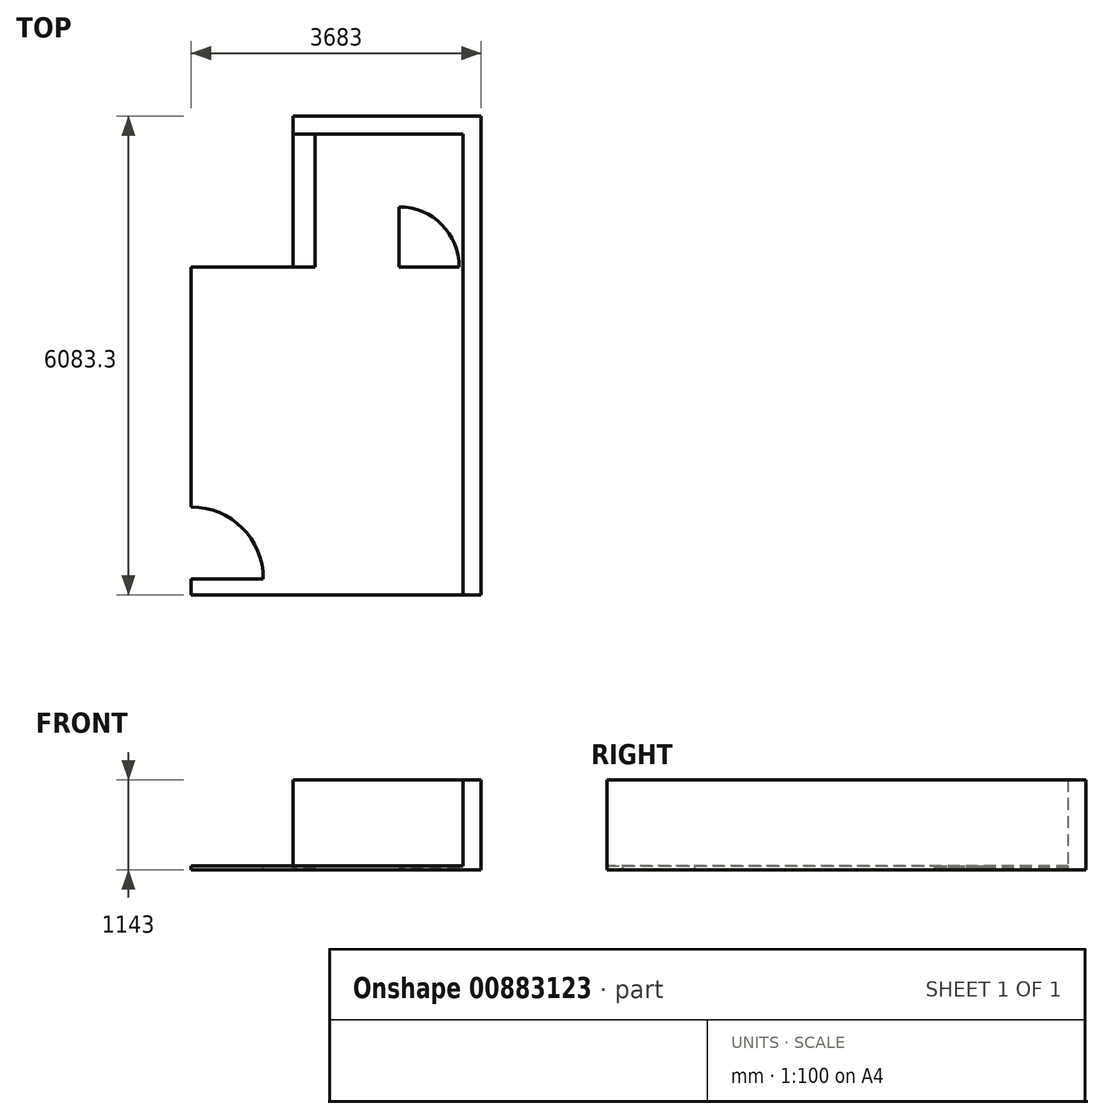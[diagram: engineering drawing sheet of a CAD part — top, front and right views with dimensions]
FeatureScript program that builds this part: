
annotation { "Feature Type Name" : "Feature", "Feature Type Description" : "" }
export const myFeature = defineFeature(function(context is Context, id is Id, definition is map)
    precondition{}
    {
        {
            var Q0;
            Q0=qCreatedBy(makeId("Top.planeOp"),FACE);
            var sketch = newSketch(context, id + "F0", { "sketchPlane" : qUnion([Q0])});
            skLineSegment(sketch, "E0.bottom", {"start": v(0, 0) * mm, "end": v(-3683, 0) * mm});
            skLineSegment(sketch, "E0.top", {"start": v(0, 4165.6) * mm, "end": v(-3683, 4165.6) * mm});
            skLineSegment(sketch, "E0.left", {"start": v(0, 0) * mm, "end": v(0, 4165.6) * mm});
            skLineSegment(sketch, "E0.right", {"start": v(-3683, 0) * mm, "end": v(-3683, 4165.6) * mm});
            skLineSegment(sketch, "E1", {"start": v(-228.6, 4165.6) * mm, "end": v(-228.6, 0) * mm});
            skArc(sketch, "E2", {"start": v(-1041.4, 4927.6) * mm, "mid": v(-502.58, 4704.42) * mm, "end": v(-279.4, 4165.6) * mm});
            skLineSegment(sketch, "E3", {"start": v(-1041.4, 4165.6) * mm, "end": v(-1041.4, 4927.6) * mm});
            skLineSegment(sketch, "E4", {"start": v(0, 4165.6) * mm, "end": v(0, 6083.3) * mm});
            skLineSegment(sketch, "E5", {"start": v(0, 6083.3) * mm, "end": v(-2387.6, 6083.3) * mm});
            skLineSegment(sketch, "E6", {"start": v(-2387.6, 6083.3) * mm, "end": v(-2387.6, 4165.6) * mm});
            skLineSegment(sketch, "E7", {"start": v(-228.6, 4165.6) * mm, "end": v(-228.6, 6083.3) * mm});
            skLineSegment(sketch, "E8", {"start": v(-228.6, 5854.7) * mm, "end": v(-2387.6, 5854.7) * mm});
            skLineSegment(sketch, "E9", {"start": v(-2108.2, 5854.7) * mm, "end": v(-2108.2, 4165.6) * mm});
            skArc(sketch, "E10", {"start": v(-3683, 1117.6) * mm, "mid": v(-3036.42, 849.78) * mm, "end": v(-2768.6, 203.2) * mm});
            skLineSegment(sketch, "E11", {"start": v(-3683, 203.2) * mm, "end": v(-2768.6, 203.2) * mm});
            skSolve(sketch);
        }
        {
            var Q0;
            {var subQ9=sQuery(id+"F0.wireOp",EDGE,"E1");Q0=makeQuery(id+"F0.imprint","IMPRINT",FACE,{"disambiguationData":[TD([[makeQuery(id+"F0.imprint","IMPRINT",EDGE,{"derivedFrom":subQ9}),-1.0]])]});}
            var Q1;
            {var subQ0=sQuery(id+"F0.wireOp",EDGE,"E10");Q1=makeQuery(id+"F0.imprint","IMPRINT",FACE,{"disambiguationData":[TD([[makeQuery(id+"F0.imprint","IMPRINT",EDGE,{"derivedFrom":subQ0}),-1.0]])]});}
            var Q2;
            {var subQ0=sQuery(id+"F0.wireOp",EDGE,"E0.left");Q2=makeQuery(id+"F0.imprint","IMPRINT",FACE,{"disambiguationData":[TD([[makeQuery(id+"F0.imprint","IMPRINT",EDGE,{"derivedFrom":subQ0}),1.0]])]});}
            var Q3;
            {var subQ1=sQuery(id+"F0.wireOp",EDGE,"E4");Q3=makeQuery(id+"F0.imprint","IMPRINT",FACE,{"disambiguationData":[TD([[makeQuery(id+"F0.imprint","IMPRINT",EDGE,{"derivedFrom":subQ1}),1.0]])]});}
            var Q4;
            {var subQ4=sQuery(id+"F0.wireOp",EDGE,"E2");Q4=makeQuery(id+"F0.imprint","IMPRINT",FACE,{"disambiguationData":[TD([[makeQuery(id+"F0.imprint","IMPRINT",EDGE,{"derivedFrom":subQ4}),1.0]])]});}
            var Q5;
            {var subQ0=sQuery(id+"F0.wireOp",EDGE,"E2");Q5=makeQuery(id+"F0.imprint","IMPRINT",FACE,{"disambiguationData":[TD([[makeQuery(id+"F0.imprint","IMPRINT",EDGE,{"derivedFrom":subQ0}),-1.0]])]});}
            var Q6;
            {var subQ1=sQuery(id+"F0.wireOp",EDGE,"E5");var subQ5=sQuery(id+"F0.wireOp",EDGE,"E6");var subQ6=makeQuery(id+"F0.imprint","INTERSECT",VERTEX,{"derivedFrom":[subQ1,subQ5]});Q6=makeQuery(id+"F0.imprint","IMPRINT",FACE,{"disambiguationData":[TD([[makeQuery(id+"F0.imprint","IMPRINT",EDGE,{"disambiguationData":[TD([[subQ6,1.0]])],"derivedFrom":subQ1}),1.0]])]});}
            var Q7;
            {var subQ3=sQuery(id+"F0.wireOp",EDGE,"E9");Q7=makeQuery(id+"F0.imprint","IMPRINT",FACE,{"disambiguationData":[TD([[makeQuery(id+"F0.imprint","IMPRINT",EDGE,{"derivedFrom":subQ3}),-1.0]])]});}
            extrude(context, id + "F1", {"entities" : qUnion([Q0, Q1, Q2, Q3, Q4, Q5, Q6, Q7]), "oppositeDirection" : true, "depth" : 25.4 * mm, "offsetDistance" : 25.4 * mm});
        }
        {
            var Q0;
            {var subQ0=sQuery(id+"F0.wireOp",EDGE,"E10");Q0=makeQuery(id+"F0.imprint","IMPRINT",FACE,{"disambiguationData":[TD([[makeQuery(id+"F0.imprint","IMPRINT",EDGE,{"derivedFrom":subQ0}),-1.0]])]});}
            var Q1;
            {var subQ0=sQuery(id+"F0.wireOp",EDGE,"E2");Q1=makeQuery(id+"F0.imprint","IMPRINT",FACE,{"disambiguationData":[TD([[makeQuery(id+"F0.imprint","IMPRINT",EDGE,{"derivedFrom":subQ0}),-1.0]])]});}
            extrude(context, id + "F2", {"entities" : qUnion([Q0, Q1]), "operationType" : NewBodyOperationType.ADD, "depth" : 25.4 * mm, "offsetDistance" : 25.4 * mm});
        }
        {
            var Q0;
            {var subQ1=sQuery(id+"F0.wireOp",EDGE,"E4");Q0=makeQuery(id+"F0.imprint","IMPRINT",FACE,{"disambiguationData":[TD([[makeQuery(id+"F0.imprint","IMPRINT",EDGE,{"derivedFrom":subQ1}),1.0]])]});}
            var Q1;
            {var subQ0=sQuery(id+"F0.wireOp",EDGE,"E0.left");Q1=makeQuery(id+"F0.imprint","IMPRINT",FACE,{"disambiguationData":[TD([[makeQuery(id+"F0.imprint","IMPRINT",EDGE,{"derivedFrom":subQ0}),1.0]])]});}
            var Q2;
            {var subQ1=sQuery(id+"F0.wireOp",EDGE,"E5");var subQ5=sQuery(id+"F0.wireOp",EDGE,"E6");var subQ6=makeQuery(id+"F0.imprint","INTERSECT",VERTEX,{"derivedFrom":[subQ1,subQ5]});Q2=makeQuery(id+"F0.imprint","IMPRINT",FACE,{"disambiguationData":[TD([[makeQuery(id+"F0.imprint","IMPRINT",EDGE,{"disambiguationData":[TD([[subQ6,1.0]])],"derivedFrom":subQ1}),1.0]])]});}
            extrude(context, id + "F3", {"entities" : qUnion([Q0, Q1, Q2]), "operationType" : NewBodyOperationType.ADD, "depth" : 1117.6 * mm, "offsetDistance" : 25.4 * mm});
        }
        {
            var Q0;
            Q0=sQuery(id+"F0.wireOp",EDGE,"E0.top");
            var Q1;
            Q1=sQuery(id+"F0.wireOp",EDGE,"E0.right");
            var Q2;
            Q2=sQuery(id+"F0.wireOp",EDGE,"E0.bottom");
            var Q3;
            Q3=sQuery(id+"F0.wireOp",EDGE,"E0.left");
            extrude(context, id + "F4", {"bodyType" : ToolBodyType.SURFACE, "surfaceEntities" : qUnion([Q0, Q1, Q2, Q3]), "depth" : 2438.4 * mm, "offsetDistance" : 25.4 * mm});
        }
        {
            var Q0;
            Q0=sQuery(id+"F0.wireOp",EDGE,"E6");
            var Q1;
            Q1=sQuery(id+"F0.wireOp",EDGE,"E5");
            var Q2;
            Q2=sQuery(id+"F0.wireOp",EDGE,"E4");
            extrude(context, id + "F5", {"bodyType" : ToolBodyType.SURFACE, "surfaceEntities" : qUnion([Q0, Q1, Q2]), "depth" : 2438.4 * mm, "offsetDistance" : 25.4 * mm});
        }
    });
